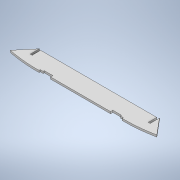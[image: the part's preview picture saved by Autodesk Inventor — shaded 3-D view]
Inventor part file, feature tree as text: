
AUTODESK INVENTOR PART (.ipt)
format: ipt  version: 2020.3 (Build 243373010, 373A)  size: 143,872 bytes
history: native  units: in
note: dims shown in document units (in); Inventor stores cm internally (conversion verified against a paired STEP export)
features: other x3, extrude x1, mirror x1, sketch x1
ambient origin geometry x8: Origin, YZ Plane, XZ Plane, XY Plane, X Axis, Y Axis, Z Axis, Center Point
bodies: Solid1 (feature_tree)
feature tree (6):
  other  "transom"
  other  "base_sketch.ipt"
  extrude  "Extrusion1"  Depth=0.0787in
  mirror  "Mirror1"
  other  "transom_plane"
  sketch  "Sketch2"  dims[d0=0.3937in d1=0.0787in d2=0.0787in d3=0.0in d4=0.0472in d5=0.0472in d6=0.2362in d7=0.2362in]
